# Revit family: Drinking_Fountain-Oasis-Radii_Modular-M8WR
name_source: partatom
category: Plumbing Fixtures
revit_build: Autodesk Revit MEP 2013 (Build: 20130531_2115(x64)
units: mm (PartAtom-declared; Revit-internal decimal feet)

## types (1)
- M8WR
    Apparent Load = 550 VA
    Base Rate = 8 GPM
    Chiller = Yes
    Compression HP = 0 VA
    Default Elevation = 2' - 3"
    Description = Radii Modular
    Finish = Metal - Oasis International - Brushed Stainless Steel - Exterior Finish
    Full Load Amps = 5 A
    Manufacturer = Oasis International
    Manufacturer Fax Number = (614)322-4557
    Metal Finish = Metal - Oasis International - Brushed Stainless Steel - Exterior Finish
    Model = M8WR
    Number of Poles = 1
    Power Factor = 1
    Pre Cooler = No
    Product Documentation Link = http://www.oasiscoolers.com
    Product Name = Radii Fountain
    Product Page URL = http://www.oasiscoolers.com
    Rated Capacity = 8 GPM
    Rated Watts = 550 W
    URL = www.oasiscoolers.com/default.aspx
    Voltage = 115 V
    Width = 3' - 2 3/4"

## geometry (parser evidence)
native form markers: Blend x8, Sweep x22
no freeform markers — native parametric forms only
